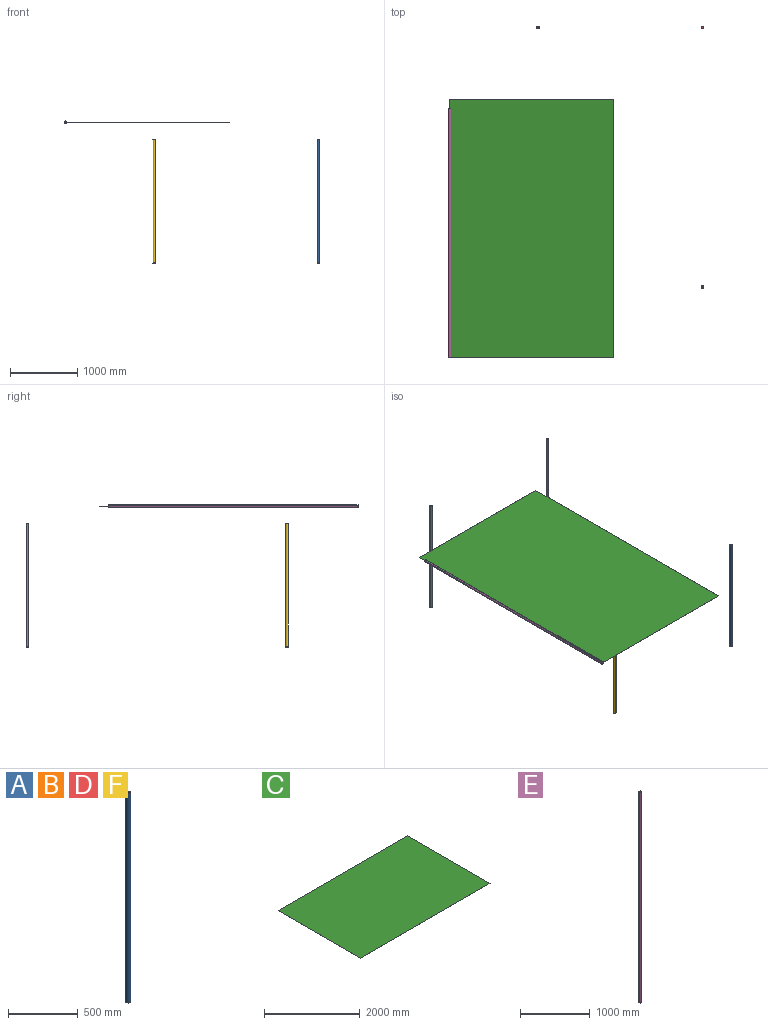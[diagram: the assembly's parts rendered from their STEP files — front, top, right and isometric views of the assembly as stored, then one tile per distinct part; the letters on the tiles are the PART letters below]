
ASSEMBLY  parts=6 mates=1
PART A: 5 faces, bbox 38.1x38.1x1828.8 mm
  f0: cylinder r=19.05mm len=1828.8mm, axis (0,0,-1), area 218897.6mm2, adj f1,f2
  f1: plane 38.1x38.1mm, normal (0,0,1), area 348.4mm2, adj f0,f3
  f2: plane 38.1x38.1mm, normal (0,0,-1), area 1140.1mm2, adj f0
  f3: cylinder r=15.88mm len=1825.63mm, axis (0,0,-1), area 182098mm2, adj f1,f4
  f4: plane 31.75x31.75mm, normal (0,0,1), area 791.7mm2, adj f3
PART B: same geometry as A
PART C: 6 faces, bbox 3835.4x2438.4x1.6 mm
  f0: plane 3835.4x1.59mm, normal (0,-1,0), area 6088.7mm2, adj f1,f3,f4,f5
  f1: plane 2438.4x1.59mm, normal (1,0,0), area 3871mm2, adj f0,f2,f4,f5
  f2: plane 3835.4x1.59mm, normal (0,1,0), area 6088.7mm2, adj f1,f3,f4,f5
  f3: plane 2438.4x1.59mm, normal (-1,0,0), area 3871mm2, adj f0,f2,f4,f5
  f4: plane 3835.4x2438.4mm, normal (0,0,1), area 9352239.4mm2, adj f0,f1,f2,f3
  f5: plane 3835.4x2438.4mm, normal (0,0,-1), area 9352239.4mm2, adj f0,f1,f2,f3
PART D: same geometry as A
PART E: 5 faces, bbox 38.1x38.1x3708.4 mm
  f0: cylinder r=19.05mm len=3708.4mm, axis (0,0,-1), area 443875.8mm2, adj f1,f2
  f1: plane 38.1x38.1mm, normal (0,0,1), area 348.4mm2, adj f0,f3
  f2: plane 38.1x38.1mm, normal (0,0,-1), area 1140.1mm2, adj f0
  f3: cylinder r=15.88mm len=3705.23mm, axis (0,0,-1), area 369579.8mm2, adj f1,f4
  f4: plane 31.75x31.75mm, normal (0,0,1), area 791.7mm2, adj f3
PART F: same geometry as A
PLACE A t=(2438.4,0,0)mm
PLACE B t=(0,3854.45,0)mm
PLACE C rot(axis=(0,0,1),90deg) t=(1125.39,2779.93,2089.34)mm
PLACE D t=(2438.4,3854.45,0)mm
PLACE E rot(axis=(-1,0,0),90deg) t=(-1313.01,-1055.47,2090.13)mm
PLACE F at identity
MATE fastened E.f0 <-> C.f3  axis (0,-1,0) through (-1313.01,-1055.47,2090.13)mm
